# Revit family: Cortadora_CK-48V_1_GENERADO
name_source: partatom
category: Equipos especializados
units: mm (PartAtom-declared; Revit-internal decimal feet)

## family parameters
Compartido = No
Corte con vacíos al cargar = No
Cota de conector redondo = Diámetro de uso
Número OmniClass = 23.21.21.31.15
Punto de cálculo de habitación = No
Se basa en plano de trabajo = No
Siempre vertical = Sí
Tipo de pieza = Normal

## types (3) — shared parameters
Comentarios de tipo = 2 in 1: high capacity vegetable cutter (650 kg/h) + cutter with 8 litre bowl.
Depth = 400 mm  [stored 1.31234 ft]
Fabricante = SAMMIC S.L.
Foodservice Equipment Identifier = Sí
HP = 2.01
Height = 652 mm  [stored 2.13911 ft]
Phase = 1
Revision Code = 1
Specification by Manufacturer = It has a variable speed motor block, large-capacity head and 8-lt cutter bowl equipped with a rotor with micro-serrated blades.
"Brushless" technology.
URL = https://www.sammic.com
URL Cutsheet = http://www.sammic.com
Watts = 1500 W
Weight in Pounds = 67.9
Width = 391 mm  [stored 1.28281 ft]
zero-valued in all types: Elevación por defecto

## per-type parameters (varying)
| type | Conn Plug | Cycle | FL Amps | Modelo | Volts |
| Combi vegetable prep.-cutter CK-48V 230/50-60/1 | EU (SCHUKO 2P+G) | 50 Hz | 10 A | 1050821 | 230 V |
| Combi vegetable prep.-cutter CK-48V 120/50-60/1 | USA (NEMA 5-15P / 2P+G) | 60 Hz | 15 A | 1050822 | 120 V |
| Combi vegetable prep.-cutter CK-48V 230/50-60/1 AUS | AU/NZ (AS 3112 10A / 2P) | 50 Hz | 10 A | 1050823 | 230 V |

note: column(s) folded — value = type name in every type: Descripción

note: [stored X ft] marks values corroborated as IEEE doubles in the binary element streams (Revit-internal decimal feet)
